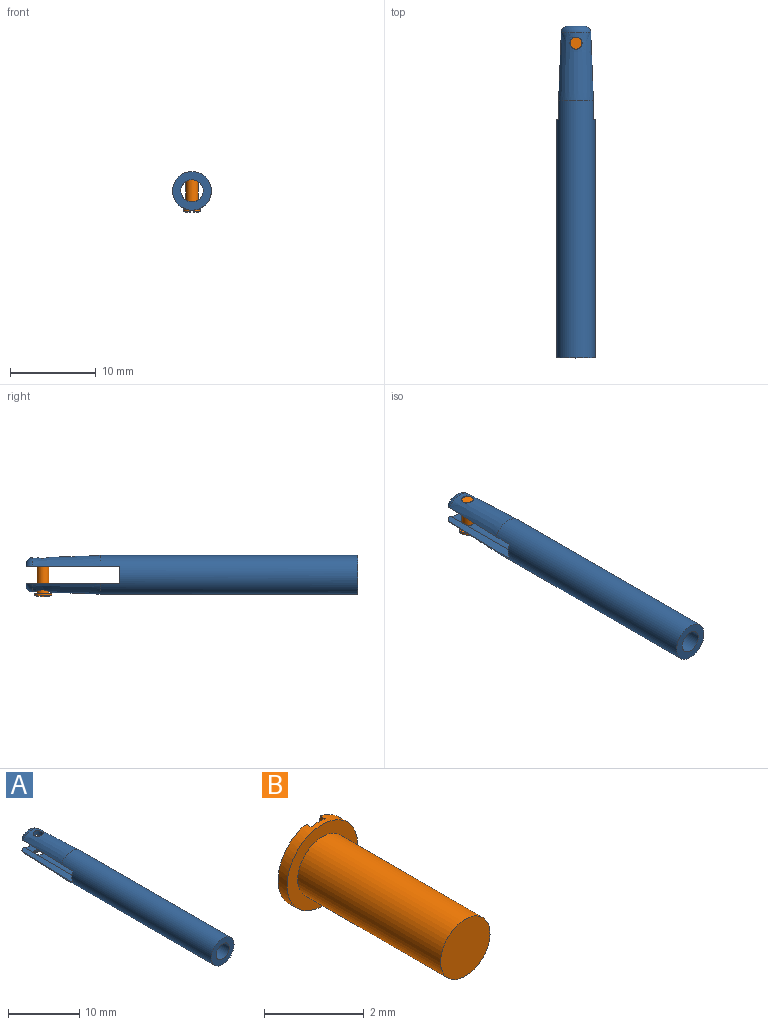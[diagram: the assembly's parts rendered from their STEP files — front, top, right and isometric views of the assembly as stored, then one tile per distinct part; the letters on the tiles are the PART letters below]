
ASSEMBLY  parts=2 mates=1
PART A: 17 faces, bbox 4.5x38.6x4.5 mm
  f0: cylinder r=1mm len=2mm, axis (0,0,1), area 2.1mm2, adj f7,f13
  f1: plane 10.91x1.2mm, normal (0,0,1), area 11.4mm2, adj f5,f7,f9,f11,f16
  f2: plane 10.91x1.2mm, normal (0,0,1), area 11.4mm2, adj f5,f7,f8,f11,f16
  f3: plane 10.91x1.2mm, normal (0,0,-1), area 11.4mm2, adj f4,f5,f9,f11,f15
  f4: cone r=2.25mm half-angle=1.9deg, axis (0,-1,0), area 34.4mm2, adj f3,f5,f10,f14,f15
  f5: cylinder r=2.25mm len=30mm, axis (0,1,0), area 414.6mm2, adj f1,f2,f3,f4,f6,f7,f8,f9
  f6: plane 4.5x4.5mm, normal (0,-1,0), area 10.6mm2, adj f5,f11
  f7: cone r=2.25mm half-angle=1.9deg, axis (0,-1,0), area 32.7mm2, adj f0,f1,f2,f5,f16
  f8: plane 2x1.42mm, normal (0,1,0), area 2mm2, adj f2,f5,f10,f11
  f9: plane 2x1.42mm, normal (0,1,0), area 2mm2, adj f1,f3,f5,f11
  f10: plane 10.91x1.2mm, normal (0,0,-1), area 11.4mm2, adj f4,f5,f8,f11,f15
  f11: cylinder r=1.3mm len=38.61mm, axis (0,1,0), area 262.4mm2, adj f1,f2,f3,f6,f8,f9,f10,f12
  f12: cylinder r=0.7mm len=1.4mm, axis (0,0,1), area 1.6mm2, adj f11,f13
  f13: plane 2x2mm, normal (0,0,-1), area 1.6mm2, adj f0,f12
  f14: cylinder r=0.7mm len=1.4mm, axis (0,0,-1), area 3.4mm2, adj f4,f11
  f15: torus R=1.23mm, axis (0,1,0), area 3.6mm2, adj f3,f4,f10,f11
  f16: torus R=1.23mm, axis (0,1,0), area 3.6mm2, adj f1,f2,f7,f11
PART B: 9 faces, bbox 2x4.4x2 mm
  f0: sphere r=4.5mm, area 1.2mm2, adj f5,f7
  f1: sphere r=4.5mm, area 1.2mm2, adj f5,f6
  f2: plane 1.4x1.4mm, normal (0,-1,0), area 1.5mm2, adj f3
  f3: cylinder r=0.7mm len=4.05mm, axis (0,1,0), area 17.8mm2, adj f2,f4
  f4: plane 2x2mm, normal (0,-1,0), area 1.6mm2, adj f3,f5
  f5: cylinder r=1mm len=2mm, axis (0,1,0), area 1.5mm2, adj f0,f1,f4,f6,f7,f8
  f6: plane 1.96x0.25mm, normal (1,0,0), area 0.4mm2, adj f1,f5,f8
  f7: plane 1.96x0.25mm, normal (-1,0,0), area 0.4mm2, adj f0,f5,f8
  f8: plane 2x0.4mm, normal (0,1,0), area 0.8mm2, adj f5,f6,f7
PLACE A t=(-4.57,-6.37,-2.99)mm fixed
PLACE B rot(axis=(-1,0,0),90deg) t=(-4.57,0.24,-1.1)mm
MATE fastened B.f3 <-> A.f0  axis (0,0,1) through (-4.57,0.24,-5.15)mm
